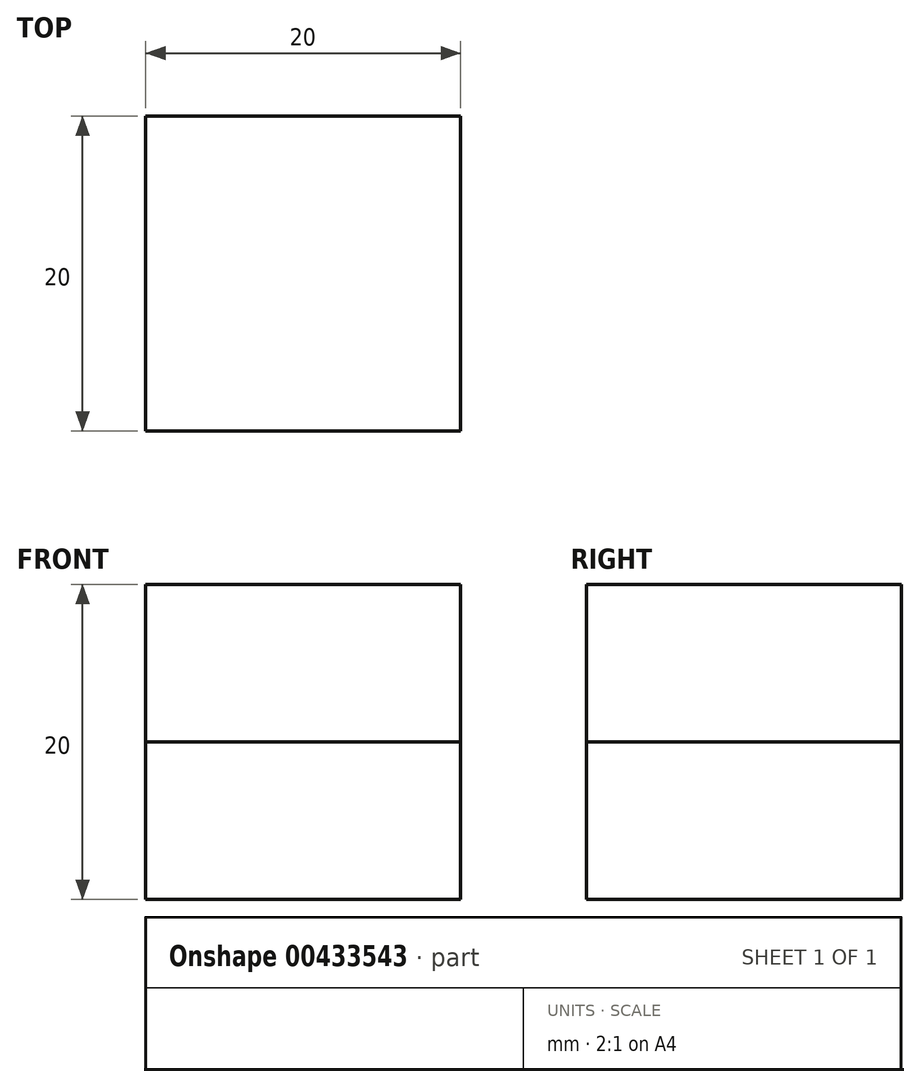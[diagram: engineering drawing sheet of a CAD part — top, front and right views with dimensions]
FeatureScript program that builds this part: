
annotation { "Feature Type Name" : "Feature", "Feature Type Description" : "" }
export const myFeature = defineFeature(function(context is Context, id is Id, definition is map)
    precondition{}
    {
        {
            var Q0;
            Q0=qCreatedBy(makeId("Top.planeOp"),FACE);
            var sketch = newSketch(context, id + "F0", { "sketchPlane" : qUnion([Q0])});
            skLineSegment(sketch, "E0.bottom", {"start": v(10, 10) * mm, "end": v(-10, 10) * mm});
            skLineSegment(sketch, "E0.top", {"start": v(10, -10) * mm, "end": v(-10, -10) * mm});
            skLineSegment(sketch, "E0.left", {"start": v(10, 10) * mm, "end": v(10, -10) * mm});
            skLineSegment(sketch, "E0.right", {"start": v(-10, 10) * mm, "end": v(-10, -10) * mm});
            skPoint(sketch, "E0.middle", {"position": v(0, 0) * mm});
            skSolve(sketch);
        }
        {
            var Q0;
            Q0=makeQuery(id+"F0.imprint","IMPRINT",FACE,{"disambiguationData":[TD([[makeQuery(id+"F0.imprint","IMPRINT",EDGE,{"derivedFrom":sQuery(id+"F0.wireOp",EDGE,"E0.bottom")}),1.0]])]});
            extrude(context, id + "F1", {"entities" : qUnion([Q0]), "depth" : 10 * mm});
        }
        {
            var Q0;
            Q0=makeQuery(id+"F1.opExtrude","CAP_FACE",FACE,{"disambiguationData":[OSD([sQuery(id+"F0.wireOp",EDGE,"E0.bottom"),sQuery(id+"F0.wireOp",EDGE,"E0.top"),sQuery(id+"F0.wireOp",EDGE,"E0.left"),sQuery(id+"F0.wireOp",EDGE,"E0.right")])],"isStart":false});
            var sketch = newSketch(context, id + "F2", { "sketchPlane" : qUnion([Q0])});
            skLineSegment(sketch, "E1.bottom", {"start": v(-10, 10) * mm, "end": v(10, 10) * mm});
            skLineSegment(sketch, "E1.top", {"start": v(-10, -10) * mm, "end": v(10, -10) * mm});
            skLineSegment(sketch, "E1.left", {"start": v(-10, 10) * mm, "end": v(-10, -10) * mm});
            skLineSegment(sketch, "E1.right", {"start": v(10, 10) * mm, "end": v(10, -10) * mm});
            skSolve(sketch);
        }
        {
            var Q0;
            Q0=makeQuery(id+"F2.imprint","IMPRINT",FACE,{"disambiguationData":[TD([[makeQuery(id+"F2.imprint","IMPRINT",EDGE,{"derivedFrom":sQuery(id+"F2.wireOp",EDGE,"E1.bottom")}),1.0]])]});
            extrude(context, id + "F3", {"entities" : qUnion([Q0]), "depth" : 10 * mm});
        }
    });
